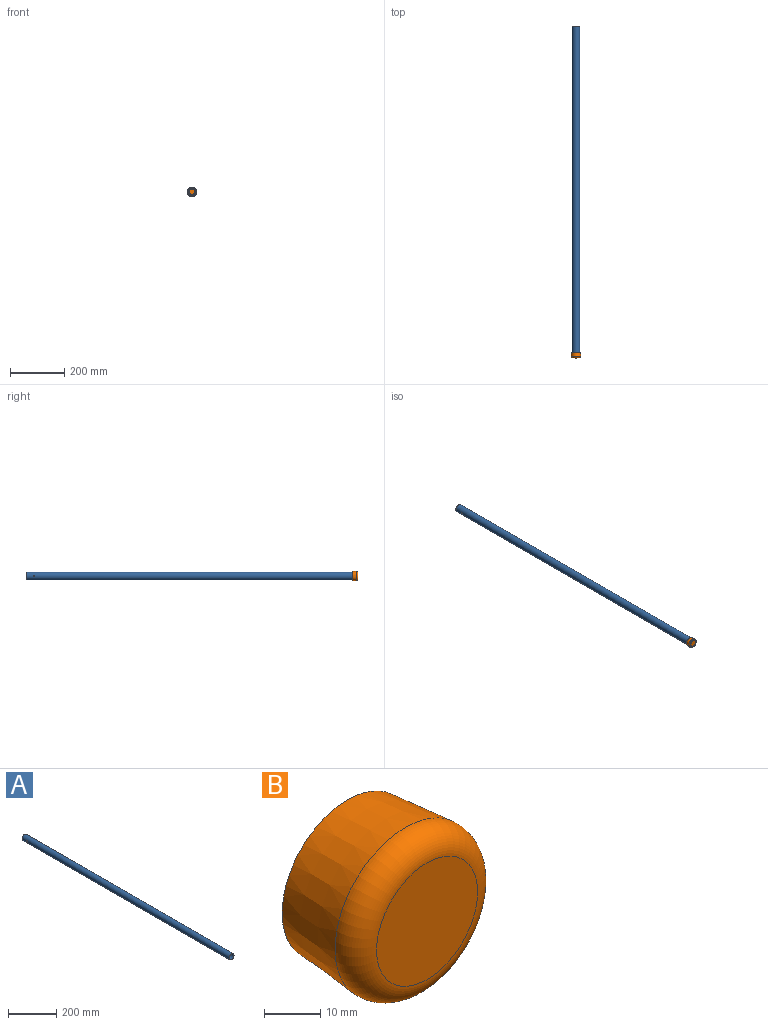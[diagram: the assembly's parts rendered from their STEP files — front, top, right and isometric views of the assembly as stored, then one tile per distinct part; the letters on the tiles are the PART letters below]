
ASSEMBLY  parts=2 mates=1
PART A: 6 faces, bbox 28.6x1220x28.6 mm
  f0: cylinder r=13.45mm len=1220mm, axis (0,1,0), area 103061.3mm2, adj f1,f3,f4,f5
  f1: plane 28.6x28.6mm, normal (0,1,0), area 74.1mm2, adj f0,f2
  f2: cylinder r=14.3mm len=1220mm, axis (0,1,0), area 109577mm2, adj f1,f3,f4,f5
  f3: plane 28.6x28.6mm, normal (0,-1,0), area 74.1mm2, adj f0,f2
  f4: cylinder r=2.5mm len=5mm, axis (1,0,0), area 13.5mm2, adj f0,f2
  f5: cylinder r=2.5mm len=5mm, axis (1,0,0), area 13.5mm2, adj f0,f2
PART B: 11 faces, bbox 38.3x20x38.3 mm
  f0: cone r=18.15mm half-angle=5deg, axis (0,-1,0), area 1565mm2, adj f8,f9
  f1: plane 25.39x25.39mm, normal (0,-1,0), area 506.2mm2, adj f9
  f2: plane 20.35x20.35mm, normal (0,1,0), area 325.3mm2, adj f3
  f3: cone r=10.44mm half-angle=5deg, axis (0,1,0), area 195mm2, adj f2,f4
  f4: plane 24.88x24.88mm, normal (0,1,0), area 143.7mm2, adj f3,f5
  f5: cone r=12.7mm half-angle=5deg, axis (0,-1,0), area 237.8mm2, adj f4,f6
  f6: plane 28.8x28.8mm, normal (0,1,0), area 144.7mm2, adj f5,f7
  f7: cylinder r=14.4mm len=28.8mm, axis (0,1,0), area 1492.9mm2, adj f6,f10
  f8: plane 32.8x32.8mm, normal (0,1,0), area 99.9mm2, adj f0,f10
  f9: torus R=12.69mm, axis (0,1,0), area 832mm2, adj f0,f1
  f10: cone r=14.4mm half-angle=45deg, axis (0,1,0), area 132.4mm2, adj f7,f8
PLACE A at identity fixed
PLACE B at identity
MATE fastened B.f0 <-> A.f0  axis (0,1,0) through (0,-1220,0)mm
